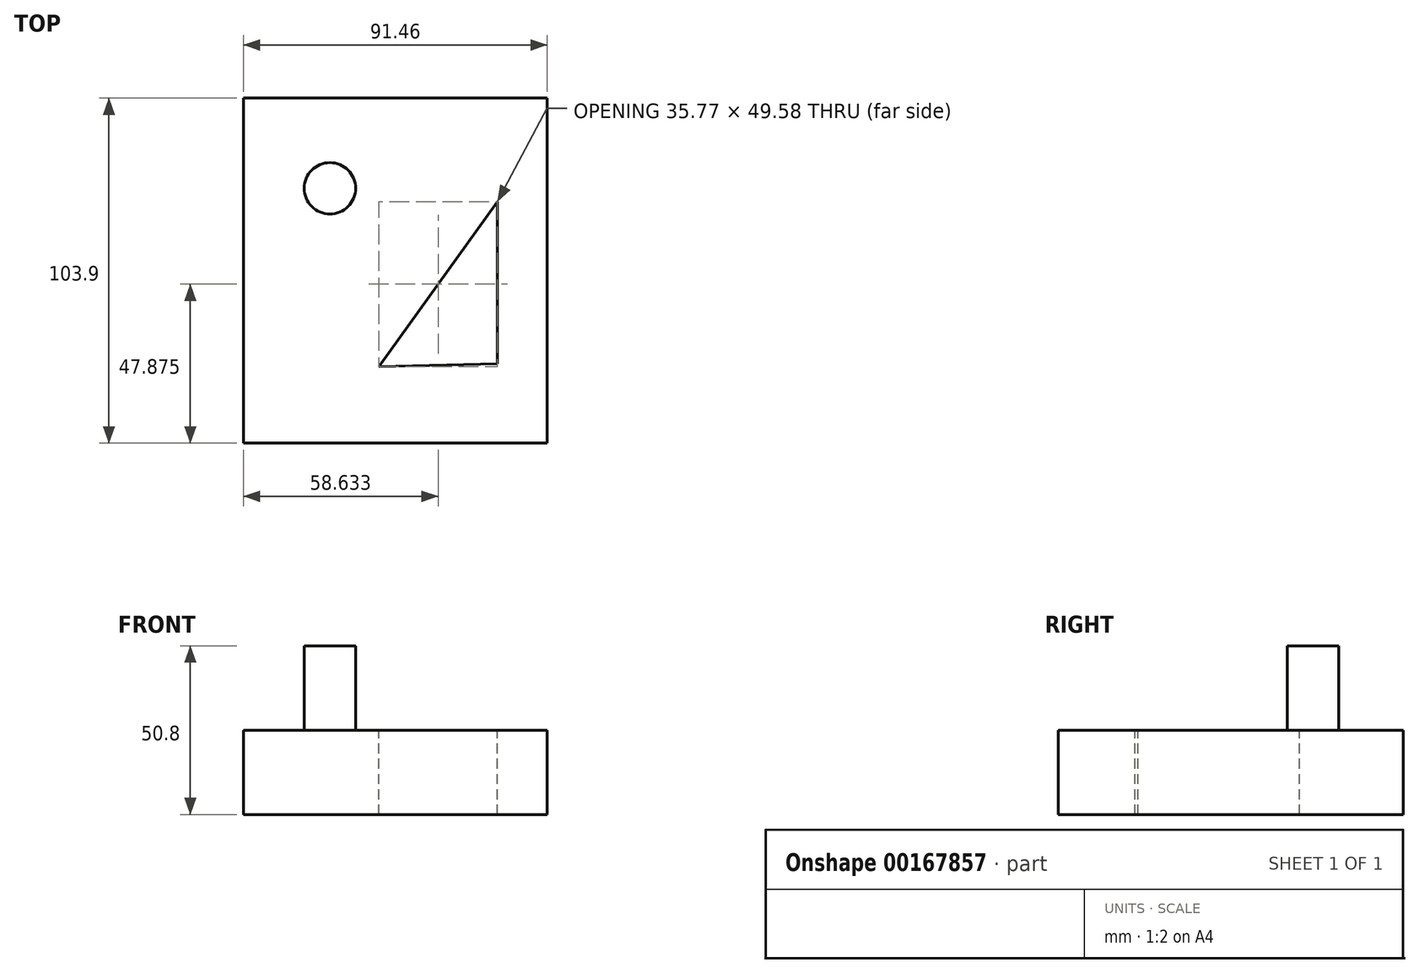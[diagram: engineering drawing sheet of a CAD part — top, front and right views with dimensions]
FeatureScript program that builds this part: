
annotation { "Feature Type Name" : "Feature", "Feature Type Description" : "" }
export const myFeature = defineFeature(function(context is Context, id is Id, definition is map)
    precondition{}
    {
        {
            var Q0;
            Q0=qCreatedBy(makeId("Top.planeOp"),FACE);
            var sketch = newSketch(context, id + "F0", { "sketchPlane" : qUnion([Q0])});
            skLineSegment(sketch, "E0.bottom", {"start": v(45.73, 51.95) * mm, "end": v(-45.73, 51.95) * mm});
            skLineSegment(sketch, "E0.top", {"start": v(45.73, -51.95) * mm, "end": v(-45.73, -51.95) * mm});
            skLineSegment(sketch, "E0.left", {"start": v(45.73, 51.95) * mm, "end": v(45.73, -51.95) * mm});
            skLineSegment(sketch, "E0.right", {"start": v(-45.73, 51.95) * mm, "end": v(-45.73, -51.95) * mm});
            skPoint(sketch, "E0.middle", {"position": v(0, 0) * mm});
            skSolve(sketch);
        }
        {
            var Q0;
            Q0 = qSketchRegion(id + "F0", true);
            extrude(context, id + "F1", {"entities" : qUnion([Q0]), "depth" : 25.4 * mm});
        }
        {
            var Q0;
            Q0=makeQuery(id+"F1.opExtrude","CAP_FACE",FACE,{"disambiguationData":[OSD([sQuery(id+"F0.wireOp",EDGE,"E0.bottom"),sQuery(id+"F0.wireOp",EDGE,"E0.top"),sQuery(id+"F0.wireOp",EDGE,"E0.left"),sQuery(id+"F0.wireOp",EDGE,"E0.right")])],"isStart":false});
            var sketch = newSketch(context, id + "F2", { "sketchPlane" : qUnion([Q0])});
            skCircle(sketch, "E1", {"center": v(-19.7, 24.79) * mm, "radius": 7.74 * mm});
            skLineSegment(sketch, "E2", {"start": v(-4.98, -28.86) * mm, "end": v(30.79, 20.71) * mm});
            skLineSegment(sketch, "E3", {"start": v(30.79, 20.71) * mm, "end": v(30.79, -27.96) * mm});
            skLineSegment(sketch, "E4", {"start": v(30.79, -27.96) * mm, "end": v(-4.98, -28.86) * mm});
            skSolve(sketch);
        }
        {
            var Q0;
            Q0=makeQuery(id+"F2.imprint","IMPRINT",FACE,{"disambiguationData":[TD([[makeQuery(id+"F2.imprint","IMPRINT",EDGE,{"derivedFrom":sQuery(id+"F2.wireOp",EDGE,"E1")}),1.0]])]});
            extrude(context, id + "F3", {"entities" : qUnion([Q0]), "operationType" : NewBodyOperationType.ADD, "depth" : 25.4 * mm});
        }
        {
            var Q0;
            Q0=makeQuery(id+"F2.imprint","IMPRINT",FACE,{"disambiguationData":[TD([[makeQuery(id+"F2.imprint","IMPRINT",EDGE,{"derivedFrom":sQuery(id+"F2.wireOp",EDGE,"E2")}),-1.0]])]});
            extrude(context, id + "F4", {"entities" : qUnion([Q0]), "operationType" : NewBodyOperationType.REMOVE, "oppositeDirection" : true, "depth" : 25.4 * mm});
        }
    });
